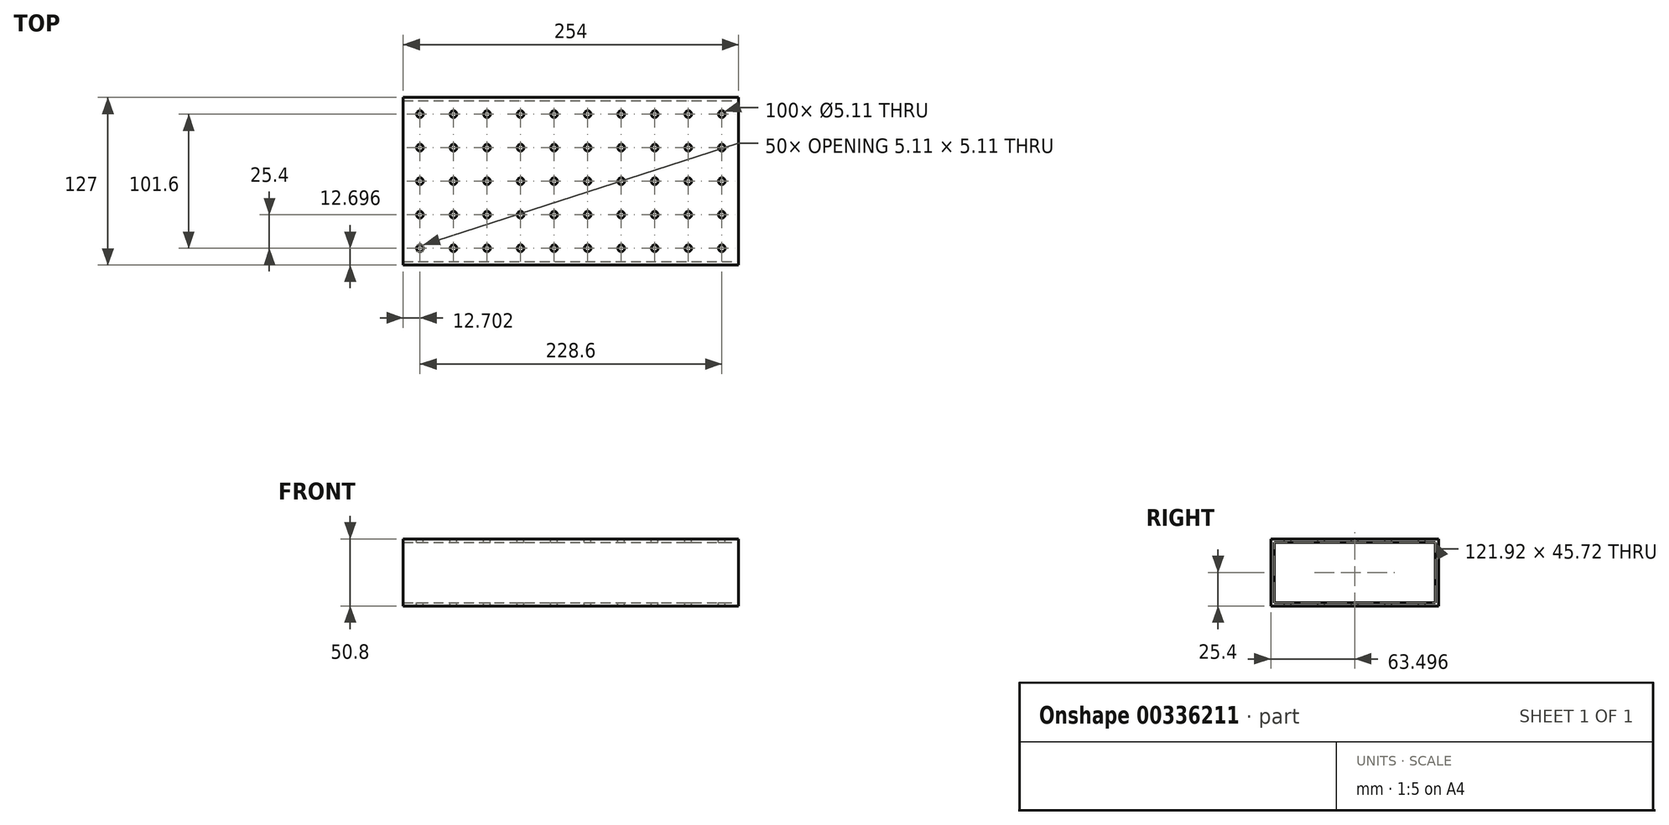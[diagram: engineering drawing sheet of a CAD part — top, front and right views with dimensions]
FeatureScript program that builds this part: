
annotation { "Feature Type Name" : "Feature", "Feature Type Description" : "" }
export const myFeature = defineFeature(function(context is Context, id is Id, definition is map)
    precondition{}
    {
        {
            var Q0;
            Q0=qCreatedBy(makeId("Top.planeOp"),FACE);
            var sketch = newSketch(context, id + "F0", { "sketchPlane" : qUnion([Q0])});
            skLineSegment(sketch, "E0.bottom", {"start": v(-123.89, 111.1) * mm, "end": v(130.11, 111.1) * mm});
            skLineSegment(sketch, "E0.top", {"start": v(-123.89, -15.9) * mm, "end": v(130.11, -15.9) * mm});
            skLineSegment(sketch, "E0.left", {"start": v(-123.89, 111.1) * mm, "end": v(-123.89, -15.9) * mm});
            skLineSegment(sketch, "E0.right", {"start": v(130.11, 111.1) * mm, "end": v(130.11, -15.9) * mm});
            skSolve(sketch);
        }
        {
            var Q0;
            Q0 = qSketchRegion(id + "F0", true);
            extrude(context, id + "F1", {"entities" : qUnion([Q0]), "depth" : 50.8 * mm});
        }
        {
            var Q0;
            Q0=makeQuery(id+"F1.opExtrude","SWEPT_FACE",FACE,{"disambiguationData":[OSD([sQuery(id+"F0.wireOp",EDGE,"E0.right")])]});
            var sketch = newSketch(context, id + "F2", { "sketchPlane" : qUnion([Q0])});
            skLineSegment(sketch, "E1.bottom", {"start": v(-13.35, 48.26) * mm, "end": v(108.57, 48.26) * mm});
            skLineSegment(sketch, "E1.top", {"start": v(-13.35, 2.54) * mm, "end": v(108.57, 2.54) * mm});
            skLineSegment(sketch, "E1.left", {"start": v(-13.35, 48.26) * mm, "end": v(-13.35, 2.54) * mm});
            skLineSegment(sketch, "E1.right", {"start": v(108.57, 48.26) * mm, "end": v(108.57, 2.54) * mm});
            skSolve(sketch);
        }
        {
            var Q0;
            Q0 = qSketchRegion(id + "F2", true);
            extrude(context, id + "F3", {"entities" : qUnion([Q0]), "operationType" : NewBodyOperationType.REMOVE, "endBound" : BoundingType.THROUGH_ALL, "oppositeDirection" : true, "depth" : 25.4 * mm});
        }
        {
            var Q0;
            Q0=makeQuery(id+"F1.opExtrude","CAP_FACE",FACE,{"disambiguationData":[OSD([sQuery(id+"F0.wireOp",EDGE,"E0.bottom"),sQuery(id+"F0.wireOp",EDGE,"E0.top"),sQuery(id+"F0.wireOp",EDGE,"E0.left"),sQuery(id+"F0.wireOp",EDGE,"E0.right")])],"isStart":false});
            var sketch = newSketch(context, id + "F4", { "sketchPlane" : qUnion([Q0])});
            skCircle(sketch, "E2", {"center": v(117.41, 98.4) * mm, "radius": 2.55 * mm});
            skCircle(sketch, "E3.0.1.0", {"center": v(117.41, 73) * mm, "radius": 2.55 * mm});
            skCircle(sketch, "E3.0.2.0", {"center": v(117.41, 47.6) * mm, "radius": 2.55 * mm});
            skCircle(sketch, "E3.0.3.0", {"center": v(117.41, 22.2) * mm, "radius": 2.55 * mm});
            skCircle(sketch, "E3.0.4.0", {"center": v(117.41, -3.2) * mm, "radius": 2.55 * mm});
            skCircle(sketch, "E3.1.0.0", {"center": v(92.01, 98.4) * mm, "radius": 2.55 * mm});
            skCircle(sketch, "E3.1.1.0", {"center": v(92.01, 73) * mm, "radius": 2.55 * mm});
            skCircle(sketch, "E3.1.2.0", {"center": v(92.01, 47.6) * mm, "radius": 2.55 * mm});
            skCircle(sketch, "E3.1.3.0", {"center": v(92.01, 22.2) * mm, "radius": 2.55 * mm});
            skCircle(sketch, "E3.1.4.0", {"center": v(92.01, -3.2) * mm, "radius": 2.55 * mm});
            skCircle(sketch, "E3.2.0.0", {"center": v(66.61, 98.4) * mm, "radius": 2.55 * mm});
            skCircle(sketch, "E3.2.1.0", {"center": v(66.61, 73) * mm, "radius": 2.55 * mm});
            skCircle(sketch, "E3.2.2.0", {"center": v(66.61, 47.6) * mm, "radius": 2.55 * mm});
            skCircle(sketch, "E3.2.3.0", {"center": v(66.61, 22.2) * mm, "radius": 2.55 * mm});
            skCircle(sketch, "E3.2.4.0", {"center": v(66.61, -3.2) * mm, "radius": 2.55 * mm});
            skCircle(sketch, "E3.3.0.0", {"center": v(41.21, 98.4) * mm, "radius": 2.55 * mm});
            skCircle(sketch, "E3.3.1.0", {"center": v(41.21, 73) * mm, "radius": 2.55 * mm});
            skCircle(sketch, "E3.3.2.0", {"center": v(41.21, 47.6) * mm, "radius": 2.55 * mm});
            skCircle(sketch, "E3.3.3.0", {"center": v(41.21, 22.2) * mm, "radius": 2.55 * mm});
            skCircle(sketch, "E3.3.4.0", {"center": v(41.21, -3.2) * mm, "radius": 2.55 * mm});
            skCircle(sketch, "E3.4.0.0", {"center": v(15.81, 98.4) * mm, "radius": 2.55 * mm});
            skCircle(sketch, "E3.4.1.0", {"center": v(15.81, 73) * mm, "radius": 2.55 * mm});
            skCircle(sketch, "E3.4.2.0", {"center": v(15.81, 47.6) * mm, "radius": 2.55 * mm});
            skCircle(sketch, "E3.4.3.0", {"center": v(15.81, 22.2) * mm, "radius": 2.55 * mm});
            skCircle(sketch, "E3.4.4.0", {"center": v(15.81, -3.2) * mm, "radius": 2.55 * mm});
            skCircle(sketch, "E3.5.0.0", {"center": v(-9.59, 98.4) * mm, "radius": 2.55 * mm});
            skCircle(sketch, "E3.5.1.0", {"center": v(-9.59, 73) * mm, "radius": 2.55 * mm});
            skCircle(sketch, "E3.5.2.0", {"center": v(-9.59, 47.6) * mm, "radius": 2.55 * mm});
            skCircle(sketch, "E3.5.3.0", {"center": v(-9.59, 22.2) * mm, "radius": 2.55 * mm});
            skCircle(sketch, "E3.5.4.0", {"center": v(-9.59, -3.2) * mm, "radius": 2.55 * mm});
            skCircle(sketch, "E3.6.0.0", {"center": v(-34.99, 98.4) * mm, "radius": 2.55 * mm});
            skCircle(sketch, "E3.6.1.0", {"center": v(-34.99, 73) * mm, "radius": 2.55 * mm});
            skCircle(sketch, "E3.6.2.0", {"center": v(-34.99, 47.6) * mm, "radius": 2.55 * mm});
            skCircle(sketch, "E3.6.3.0", {"center": v(-34.99, 22.2) * mm, "radius": 2.55 * mm});
            skCircle(sketch, "E3.6.4.0", {"center": v(-34.99, -3.2) * mm, "radius": 2.55 * mm});
            skCircle(sketch, "E3.7.0.0", {"center": v(-60.39, 98.4) * mm, "radius": 2.55 * mm});
            skCircle(sketch, "E3.7.1.0", {"center": v(-60.39, 73) * mm, "radius": 2.55 * mm});
            skCircle(sketch, "E3.7.2.0", {"center": v(-60.39, 47.6) * mm, "radius": 2.55 * mm});
            skCircle(sketch, "E3.7.3.0", {"center": v(-60.39, 22.2) * mm, "radius": 2.55 * mm});
            skCircle(sketch, "E3.7.4.0", {"center": v(-60.39, -3.2) * mm, "radius": 2.55 * mm});
            skCircle(sketch, "E3.8.0.0", {"center": v(-85.79, 98.4) * mm, "radius": 2.55 * mm});
            skCircle(sketch, "E3.8.1.0", {"center": v(-85.79, 73) * mm, "radius": 2.55 * mm});
            skCircle(sketch, "E3.8.2.0", {"center": v(-85.79, 47.6) * mm, "radius": 2.55 * mm});
            skCircle(sketch, "E3.8.3.0", {"center": v(-85.79, 22.2) * mm, "radius": 2.55 * mm});
            skCircle(sketch, "E3.8.4.0", {"center": v(-85.79, -3.2) * mm, "radius": 2.55 * mm});
            skCircle(sketch, "E3.9.0.0", {"center": v(-111.19, 98.4) * mm, "radius": 2.55 * mm});
            skCircle(sketch, "E3.9.1.0", {"center": v(-111.19, 73) * mm, "radius": 2.55 * mm});
            skCircle(sketch, "E3.9.2.0", {"center": v(-111.19, 47.6) * mm, "radius": 2.55 * mm});
            skCircle(sketch, "E3.9.3.0", {"center": v(-111.19, 22.2) * mm, "radius": 2.55 * mm});
            skCircle(sketch, "E3.9.4.0", {"center": v(-111.19, -3.2) * mm, "radius": 2.55 * mm});
            skLineSegment(sketch, "E3.direction1", {"start": v(117.41, 98.4) * mm, "end": v(92.01, 98.4) * mm, "construction": true});
            skLineSegment(sketch, "E3.direction2", {"start": v(117.41, 98.4) * mm, "end": v(117.41, 73) * mm, "construction": true});
            skSolve(sketch);
        }
        {
            var Q0;
            Q0=sQuery(id+"F4.wireOp",VERTEX,"E3.7.2.0.center");
            var Q1;
            Q1=sQuery(id+"F4.wireOp",VERTEX,"E3.4.1.0.center");
            var Q2;
            Q2=sQuery(id+"F4.wireOp",VERTEX,"E3.3.0.0.center");
            var Q3;
            Q3=sQuery(id+"F4.wireOp",VERTEX,"E3.9.2.0.center");
            var Q4;
            Q4=sQuery(id+"F4.wireOp",VERTEX,"E3.6.1.0.center");
            var Q5;
            Q5=sQuery(id+"F4.wireOp",VERTEX,"E3.7.3.0.center");
            var Q6;
            Q6=sQuery(id+"F4.wireOp",VERTEX,"E3.4.2.0.center");
            var Q7;
            Q7=sQuery(id+"F4.wireOp",VERTEX,"E3.3.1.0.center");
            var Q8;
            Q8=sQuery(id+"F4.wireOp",VERTEX,"E3.8.1.0.center");
            var Q9;
            Q9=sQuery(id+"F4.wireOp",VERTEX,"E3.9.3.0.center");
            var Q10;
            Q10=sQuery(id+"F4.wireOp",VERTEX,"E3.5.0.0.center");
            var Q11;
            Q11=sQuery(id+"F4.wireOp",VERTEX,"E3.6.2.0.center");
            var Q12;
            Q12=sQuery(id+"F4.wireOp",VERTEX,"E3.7.0.0.center");
            var Q13;
            Q13=sQuery(id+"F4.wireOp",VERTEX,"E3.3.4.0.center");
            var Q14;
            Q14=sQuery(id+"F4.wireOp",VERTEX,"E3.2.2.0.center");
            var Q15;
            Q15=sQuery(id+"F4.wireOp",VERTEX,"E3.8.4.0.center");
            var Q16;
            Q16=sQuery(id+"F4.wireOp",VERTEX,"E3.5.3.0.center");
            var Q17;
            Q17=sQuery(id+"F4.wireOp",VERTEX,"E3.7.4.0.center");
            var Q18;
            Q18=sQuery(id+"F4.wireOp",VERTEX,"E3.4.3.0.center");
            var Q19;
            Q19=sQuery(id+"F4.wireOp",VERTEX,"E3.1.4.0.center");
            var Q20;
            Q20=sQuery(id+"F4.wireOp",VERTEX,"E3.3.2.0.center");
            var Q21;
            Q21=sQuery(id+"F4.wireOp",VERTEX,"E3.2.0.0.center");
            var Q22;
            Q22=sQuery(id+"F4.wireOp",VERTEX,"E3.9.4.0.center");
            var Q23;
            Q23=sQuery(id+"F4.wireOp",VERTEX,"E3.8.2.0.center");
            var Q24;
            Q24=sQuery(id+"F4.wireOp",VERTEX,"E3.6.3.0.center");
            var Q25;
            Q25=sQuery(id+"F4.wireOp",VERTEX,"E3.5.1.0.center");
            var Q26;
            Q26=sQuery(id+"F4.wireOp",VERTEX,"E3.2.1.0.center");
            var Q27;
            Q27=sQuery(id+"F4.wireOp",VERTEX,"E3.2.3.0.center");
            var Q28;
            Q28=sQuery(id+"F4.wireOp",VERTEX,"E2.center");
            var Q29;
            Q29=sQuery(id+"F4.wireOp",VERTEX,"E3.0.1.0.center");
            var Q30;
            Q30=sQuery(id+"F4.wireOp",VERTEX,"E3.0.2.0.center");
            var Q31;
            Q31=sQuery(id+"F4.wireOp",VERTEX,"E3.0.3.0.center");
            var Q32;
            Q32=sQuery(id+"F4.wireOp",VERTEX,"E3.0.4.0.center");
            var Q33;
            Q33=sQuery(id+"F4.wireOp",VERTEX,"E3.1.0.0.center");
            var Q34;
            Q34=sQuery(id+"F4.wireOp",VERTEX,"E3.1.1.0.center");
            var Q35;
            Q35=sQuery(id+"F4.wireOp",VERTEX,"E3.1.2.0.center");
            var Q36;
            Q36=sQuery(id+"F4.wireOp",VERTEX,"E3.1.3.0.center");
            var Q37;
            Q37=sQuery(id+"F4.wireOp",VERTEX,"E3.9.0.0.center");
            var Q38;
            Q38=sQuery(id+"F4.wireOp",VERTEX,"E3.5.4.0.center");
            var Q39;
            Q39=sQuery(id+"F4.wireOp",VERTEX,"E3.8.0.0.center");
            var Q40;
            Q40=sQuery(id+"F4.wireOp",VERTEX,"E3.4.4.0.center");
            var Q41;
            Q41=sQuery(id+"F4.wireOp",VERTEX,"E3.7.1.0.center");
            var Q42;
            Q42=sQuery(id+"F4.wireOp",VERTEX,"E3.4.0.0.center");
            var Q43;
            Q43=sQuery(id+"F4.wireOp",VERTEX,"E3.3.3.0.center");
            var Q44;
            Q44=sQuery(id+"F4.wireOp",VERTEX,"E3.8.3.0.center");
            var Q45;
            Q45=sQuery(id+"F4.wireOp",VERTEX,"E3.5.2.0.center");
            var Q46;
            Q46=sQuery(id+"F4.wireOp",VERTEX,"E3.6.4.0.center");
            var Q47;
            Q47=sQuery(id+"F4.wireOp",VERTEX,"E3.2.4.0.center");
            var Q48;
            Q48=sQuery(id+"F4.wireOp",VERTEX,"E3.9.1.0.center");
            var Q49;
            Q49=sQuery(id+"F4.wireOp",VERTEX,"E3.6.0.0.center");
            var Q50;
            Q50=makeQuery(id+"F1.opExtrude","SWEPT_BODY",BODY,{"disambiguationData":[OSD([sQuery(id+"F0.wireOp",EDGE,"E0.bottom"),sQuery(id+"F0.wireOp",EDGE,"E0.top"),sQuery(id+"F0.wireOp",EDGE,"E0.left"),sQuery(id+"F0.wireOp",EDGE,"E0.right")])]});
            hole(context, id + "F5", {"style" : HoleStyle.SIMPLE, "endStyle" : HoleEndStyle.THROUGH, "holeDiameter" : 5.1 * mm, "tappedDepth" : 12.7 * mm, "tapClearance" : 3, "locations" : qUnion([Q0, Q1, Q2, Q3, Q4, Q5, Q6, Q7, Q8, Q9, Q10, Q11, Q12, Q13, Q14, Q15, Q16, Q17, Q18, Q19, Q20, Q21, Q22, Q23, Q24, Q25, Q26, Q27, Q28, Q29, Q30, Q31, Q32, Q33, Q34, Q35, Q36, Q37, Q38, Q39, Q40, Q41, Q42, Q43, Q44, Q45, Q46, Q47, Q48, Q49]), "scope" : qUnion([Q50])});
        }
    });
